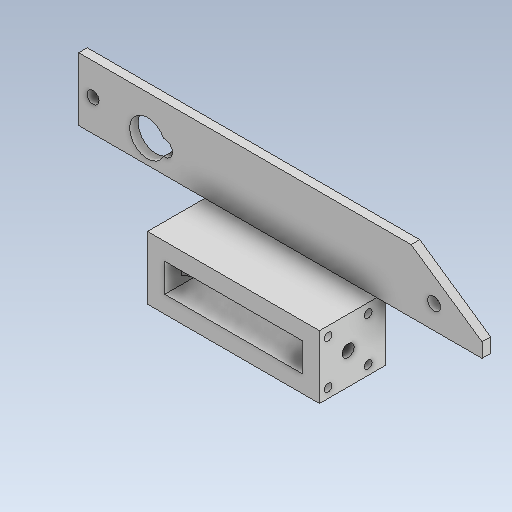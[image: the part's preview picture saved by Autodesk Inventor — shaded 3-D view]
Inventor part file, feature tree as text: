
AUTODESK INVENTOR PART (.ipt)
format: ipt  version: 2020 (Build 240168000, 168)  size: 190,464 bytes
history: native  units: mm
features: sketch x6, other x4, extrude x1
ambient origin geometry x8: Origin, YZ Plane, XZ Plane, XY Plane, X Axis, Y Axis, Z Axis, Center Point
bodies: Body1 (feature_tree)
feature tree (11):
  other  "wheel-adapter.ipt"
  extrude  "Wyciągnięcie proste1"  Depth=10.0mm
  other  "Bryła1::wheel-adapter.ipt"
  other  "Bryła wyprowadzona1"
  sketch  "Szkic1"
  sketch  "Szkic2"
  sketch  "Szkic4"
  sketch  "Szkic5"
  sketch  "Szkic6"
  sketch  "Szkic7"
  other  "Bryła1"
